# Revit family: Tray_Rack_CB-33_BIM
name_source: partatom
category: Arredi
units: mm (PartAtom-declared; Revit-internal decimal feet)

## family parameters
Attiva taglio nelle viste = No
Basato su piano di lavoro = No
Condiviso = No
Numero OmniClass = 23.40.20.00
Origine composizione di rendering = Geometria famiglia
Punto di calcolo locali = No
Sempre verticale = Sì
Taglio con vuoti quando caricato = No
Titolo OmniClass = General Furniture and Specialties

## types (1)
- CB-33
    AVAILABLE FINISHES = Ebonized black lacquer on Ash (EB) or bleached, white pigment, matte acrylic on Ash (BL). Raw effect lacquer on Oak (RE). Hand rubbed natural oil on Oak or Walnut (NA), or hand rubbed black oil on Walnut (BO).
    BASE MATERIAL = BASSAM_FELLOWS_WALNUT_BLACK_OIL_W-BO
    BIM BADGE = https://bim.archiproducts.com
    COLLECTION = Tray Rack
    DEPTH = 430 mm  [stored 1.41076 ft]
    Descrizione = Solid wood side table with removable trays
    HEIGHT = 435 mm  [stored 1.42717 ft]
    MATERIAL DESCRIPTION = Carved, solid wood. Solid brass tray supports.
    Modello = Tray Rack Side Table
    PRODUCT CODE = CB-33
    PRODUCT SHEET = https://www.archiproducts.com
    Produttore = BassamFellows
    Prospetto di default = 0 mm  [stored 0 ft]
    STRUCTURE MATERIAL = BASSAM_FELLOWS_WALNUT_BLACK_OIL_W-BO
    TECHNICAL SHEET = https://bassamfellows.com
    URL = https://bassamfellows.com
    WIDTH = 625 mm  [stored 2.05052 ft]

note: [stored X ft] marks values corroborated as IEEE doubles in the binary element streams (Revit-internal decimal feet)

## geometry (parser evidence)
native form markers: Sweep x3
no freeform markers — native parametric forms only
